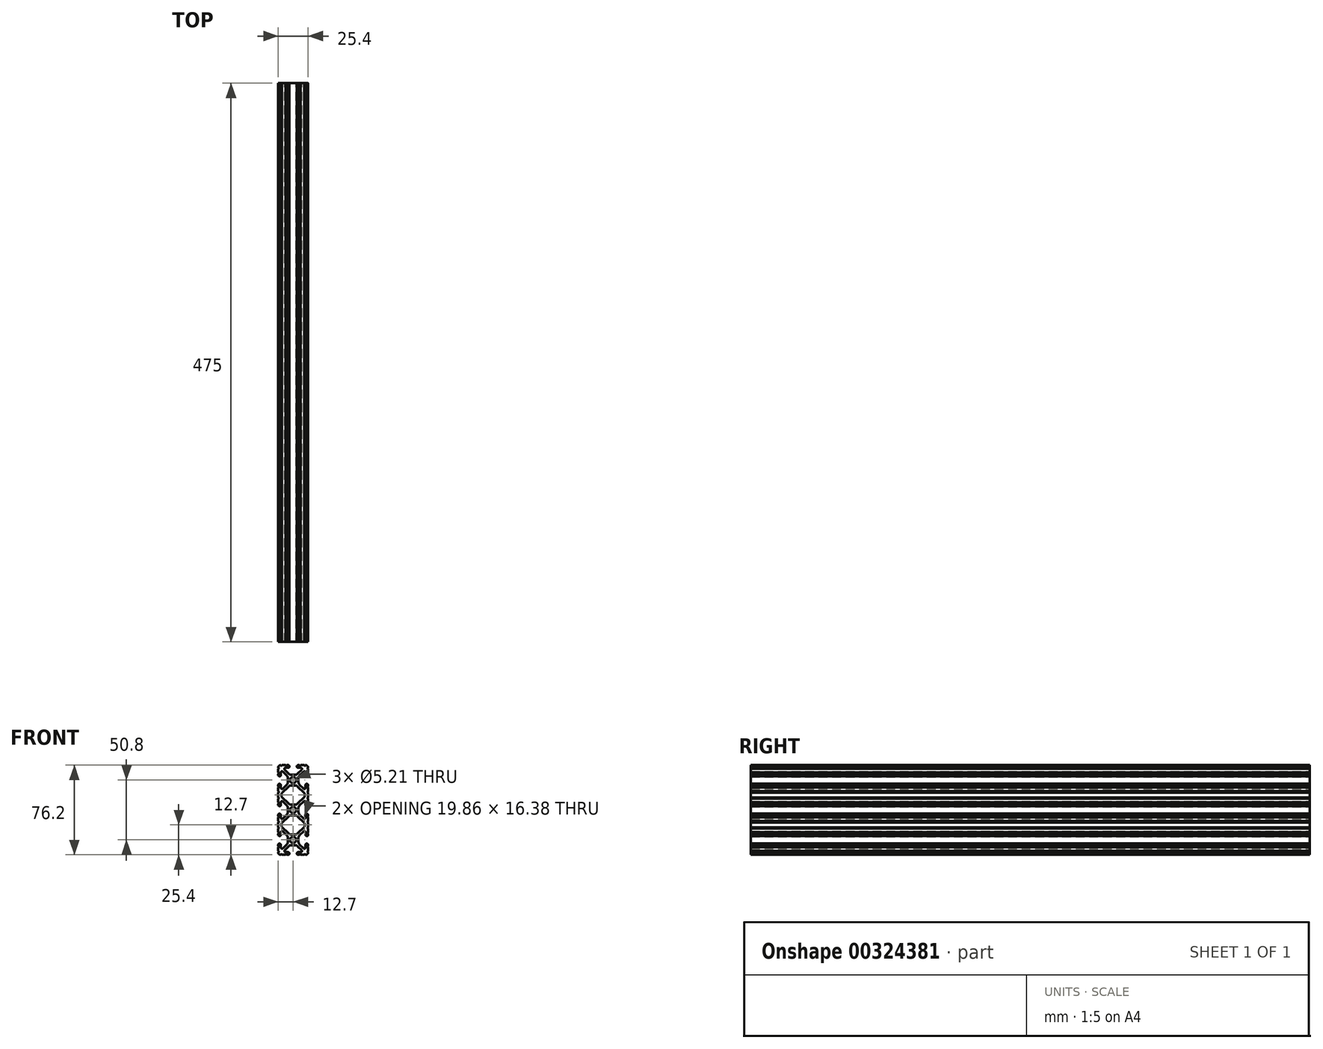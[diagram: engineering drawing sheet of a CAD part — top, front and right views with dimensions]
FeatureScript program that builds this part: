
annotation { "Feature Type Name" : "Feature", "Feature Type Description" : "" }
export const myFeature = defineFeature(function(context is Context, id is Id, definition is map)
    precondition{}
    {
        {
            var Q0;
            Q0=qCreatedBy(makeId("Front.planeOp"),FACE);
            var sketch = newSketch(context, id + "F0", { "sketchPlane" : qUnion([Q0])});
            skArc(sketch, "E0", {"start": v(2.6, 25.4) * mm, "mid": v(0, 28) * mm, "end": v(-2.6, 25.4) * mm});
            skArc(sketch, "E1", {"start": v(-2.6, 25.4) * mm, "mid": v(0, 22.8) * mm, "end": v(2.6, 25.4) * mm});
            skArc(sketch, "E2", {"start": v(-10.57, 38.1) * mm, "mid": v(-10.06, 37.6) * mm, "end": v(-9.55, 38.1) * mm});
            skArc(sketch, "E3", {"start": v(-10.57, 38.1) * mm, "mid": v(-12.08, 37.48) * mm, "end": v(-12.7, 35.97) * mm});
            skArc(sketch, "E4", {"start": v(-12.7, 34.95) * mm, "mid": v(-12.2, 35.46) * mm, "end": v(-12.7, 35.97) * mm});
            skLineSegment(sketch, "E5", {"start": v(-12.7, 34.95) * mm, "end": v(-12.7, 31.72) * mm});
            skArc(sketch, "E6", {"start": v(-12.7, 30.7) * mm, "mid": v(-12.2, 31.22) * mm, "end": v(-12.7, 31.72) * mm});
            skLineSegment(sketch, "E7", {"start": v(-12.7, 30.7) * mm, "end": v(-12.7, 29.7) * mm});
            skArc(sketch, "E8", {"start": v(-12.7, 29.7) * mm, "mid": v(-11.6, 28.6) * mm, "end": v(-10.5, 29.7) * mm});
            skLineSegment(sketch, "E9", {"start": v(-10.5, 29.7) * mm, "end": v(-10.5, 31.87) * mm});
            skArc(sketch, "E10", {"start": v(-8.76, 32.6) * mm, "mid": v(-9.86, 32.81) * mm, "end": v(-10.5, 31.87) * mm});
            skLineSegment(sketch, "E11", {"start": v(-8.76, 32.6) * mm, "end": v(-5.44, 29.28) * mm});
            skArc(sketch, "E12", {"start": v(-4.5, 27.03) * mm, "mid": v(-4.75, 28.25) * mm, "end": v(-5.44, 29.28) * mm});
            skLineSegment(sketch, "E13", {"start": v(-4.5, 27.03) * mm, "end": v(-4.5, 23.77) * mm});
            skArc(sketch, "E14", {"start": v(-5.44, 21.52) * mm, "mid": v(-4.75, 22.55) * mm, "end": v(-4.5, 23.77) * mm});
            skLineSegment(sketch, "E15", {"start": v(-5.44, 21.52) * mm, "end": v(-8.76, 18.2) * mm});
            skArc(sketch, "E16", {"start": v(-10.5, 18.93) * mm, "mid": v(-9.86, 17.99) * mm, "end": v(-8.76, 18.2) * mm});
            skLineSegment(sketch, "E17", {"start": v(-10.5, 18.93) * mm, "end": v(-10.5, 21.1) * mm});
            skArc(sketch, "E18", {"start": v(-10.5, 21.1) * mm, "mid": v(-11.6, 22.2) * mm, "end": v(-12.7, 21.1) * mm});
            skLineSegment(sketch, "E19", {"start": v(-12.7, 21.1) * mm, "end": v(-12.7, 20.1) * mm});
            skArc(sketch, "E20", {"start": v(-12.7, 19.08) * mm, "mid": v(-12.2, 19.58) * mm, "end": v(-12.7, 20.1) * mm});
            skLineSegment(sketch, "E21", {"start": v(-12.7, 19.08) * mm, "end": v(-12.7, 15.85) * mm});
            skArc(sketch, "E22", {"start": v(-12.7, 14.83) * mm, "mid": v(-12.2, 15.34) * mm, "end": v(-12.7, 15.85) * mm});
            skLineSegment(sketch, "E23", {"start": v(-12.7, 14.83) * mm, "end": v(-12.7, 10.57) * mm});
            skArc(sketch, "E24", {"start": v(-12.7, 9.55) * mm, "mid": v(-12.2, 10.06) * mm, "end": v(-12.7, 10.57) * mm});
            skLineSegment(sketch, "E25", {"start": v(-12.7, 9.55) * mm, "end": v(-12.7, 6.32) * mm});
            skArc(sketch, "E26", {"start": v(-12.7, 5.3) * mm, "mid": v(-12.2, 5.82) * mm, "end": v(-12.7, 6.32) * mm});
            skLineSegment(sketch, "E27", {"start": v(-12.7, 5.3) * mm, "end": v(-12.7, 4.3) * mm});
            skArc(sketch, "E28", {"start": v(-12.7, 4.3) * mm, "mid": v(-11.6, 3.2) * mm, "end": v(-10.5, 4.3) * mm});
            skLineSegment(sketch, "E29", {"start": v(-10.5, 4.3) * mm, "end": v(-10.5, 6.47) * mm});
            skArc(sketch, "E30", {"start": v(-8.76, 7.2) * mm, "mid": v(-9.86, 7.41) * mm, "end": v(-10.5, 6.47) * mm});
            skLineSegment(sketch, "E31", {"start": v(-8.76, 7.2) * mm, "end": v(-5.44, 3.88) * mm});
            skArc(sketch, "E32", {"start": v(-4.5, 1.63) * mm, "mid": v(-4.75, 2.85) * mm, "end": v(-5.44, 3.88) * mm});
            skLineSegment(sketch, "E33", {"start": v(-4.5, 1.63) * mm, "end": v(-4.5, -1.63) * mm});
            skArc(sketch, "E34", {"start": v(-5.44, -3.88) * mm, "mid": v(-4.75, -2.85) * mm, "end": v(-4.5, -1.63) * mm});
            skLineSegment(sketch, "E35", {"start": v(-5.44, -3.88) * mm, "end": v(-8.76, -7.2) * mm});
            skArc(sketch, "E36", {"start": v(-10.5, -6.47) * mm, "mid": v(-9.86, -7.41) * mm, "end": v(-8.76, -7.2) * mm});
            skLineSegment(sketch, "E37", {"start": v(-10.5, -6.47) * mm, "end": v(-10.5, -4.3) * mm});
            skArc(sketch, "E38", {"start": v(-10.5, -4.3) * mm, "mid": v(-11.6, -3.2) * mm, "end": v(-12.7, -4.3) * mm});
            skLineSegment(sketch, "E39", {"start": v(-12.7, -4.3) * mm, "end": v(-12.7, -5.3) * mm});
            skArc(sketch, "E40", {"start": v(-12.7, -6.32) * mm, "mid": v(-12.2, -5.82) * mm, "end": v(-12.7, -5.3) * mm});
            skLineSegment(sketch, "E41", {"start": v(-12.7, -6.32) * mm, "end": v(-12.7, -9.55) * mm});
            skArc(sketch, "E42", {"start": v(-12.7, -10.57) * mm, "mid": v(-12.2, -10.06) * mm, "end": v(-12.7, -9.55) * mm});
            skLineSegment(sketch, "E43", {"start": v(-12.7, -10.57) * mm, "end": v(-12.7, -14.83) * mm});
            skArc(sketch, "E44", {"start": v(-12.7, -15.85) * mm, "mid": v(-12.2, -15.34) * mm, "end": v(-12.7, -14.83) * mm});
            skLineSegment(sketch, "E45", {"start": v(-12.7, -15.85) * mm, "end": v(-12.7, -19.08) * mm});
            skArc(sketch, "E46", {"start": v(-12.7, -20.1) * mm, "mid": v(-12.2, -19.58) * mm, "end": v(-12.7, -19.08) * mm});
            skLineSegment(sketch, "E47", {"start": v(-12.7, -20.1) * mm, "end": v(-12.7, -21.1) * mm});
            skArc(sketch, "E48", {"start": v(-12.7, -21.1) * mm, "mid": v(-11.6, -22.2) * mm, "end": v(-10.5, -21.1) * mm});
            skLineSegment(sketch, "E49", {"start": v(-10.5, -21.1) * mm, "end": v(-10.5, -18.93) * mm});
            skArc(sketch, "E50", {"start": v(-8.76, -18.2) * mm, "mid": v(-9.86, -17.99) * mm, "end": v(-10.5, -18.93) * mm});
            skLineSegment(sketch, "E51", {"start": v(-8.76, -18.2) * mm, "end": v(-5.44, -21.52) * mm});
            skArc(sketch, "E52", {"start": v(-4.5, -23.77) * mm, "mid": v(-4.75, -22.55) * mm, "end": v(-5.44, -21.52) * mm});
            skLineSegment(sketch, "E53", {"start": v(-4.5, -23.77) * mm, "end": v(-4.5, -27.03) * mm});
            skArc(sketch, "E54", {"start": v(-5.44, -29.28) * mm, "mid": v(-4.75, -28.25) * mm, "end": v(-4.5, -27.03) * mm});
            skLineSegment(sketch, "E55", {"start": v(-5.44, -29.28) * mm, "end": v(-8.76, -32.6) * mm});
            skArc(sketch, "E56", {"start": v(-10.5, -31.87) * mm, "mid": v(-9.86, -32.81) * mm, "end": v(-8.76, -32.6) * mm});
            skLineSegment(sketch, "E57", {"start": v(-10.5, -31.87) * mm, "end": v(-10.5, -29.7) * mm});
            skArc(sketch, "E58", {"start": v(-10.5, -29.7) * mm, "mid": v(-11.6, -28.6) * mm, "end": v(-12.7, -29.7) * mm});
            skLineSegment(sketch, "E59", {"start": v(-12.7, -29.7) * mm, "end": v(-12.7, -30.7) * mm});
            skArc(sketch, "E60", {"start": v(-12.7, -31.72) * mm, "mid": v(-12.2, -31.22) * mm, "end": v(-12.7, -30.7) * mm});
            skLineSegment(sketch, "E61", {"start": v(-12.7, -31.72) * mm, "end": v(-12.7, -34.95) * mm});
            skArc(sketch, "E62", {"start": v(-12.7, -35.97) * mm, "mid": v(-12.2, -35.46) * mm, "end": v(-12.7, -34.95) * mm});
            skArc(sketch, "E63", {"start": v(-12.7, -35.97) * mm, "mid": v(-12.08, -37.48) * mm, "end": v(-10.57, -38.1) * mm});
            skArc(sketch, "E64", {"start": v(-9.55, -38.1) * mm, "mid": v(-10.06, -37.6) * mm, "end": v(-10.57, -38.1) * mm});
            skLineSegment(sketch, "E65", {"start": v(-9.55, -38.1) * mm, "end": v(-6.32, -38.1) * mm});
            skArc(sketch, "E66", {"start": v(-5.3, -38.1) * mm, "mid": v(-5.82, -37.6) * mm, "end": v(-6.32, -38.1) * mm});
            skLineSegment(sketch, "E67", {"start": v(-5.3, -38.1) * mm, "end": v(-4.3, -38.1) * mm});
            skArc(sketch, "E68", {"start": v(-4.3, -38.1) * mm, "mid": v(-3.2, -37) * mm, "end": v(-4.3, -35.9) * mm});
            skLineSegment(sketch, "E69", {"start": v(-4.3, -35.9) * mm, "end": v(-6.47, -35.9) * mm});
            skArc(sketch, "E70", {"start": v(-7.2, -34.16) * mm, "mid": v(-7.41, -35.26) * mm, "end": v(-6.47, -35.9) * mm});
            skLineSegment(sketch, "E71", {"start": v(-7.2, -34.16) * mm, "end": v(-3.88, -30.84) * mm});
            skArc(sketch, "E72", {"start": v(-1.63, -29.9) * mm, "mid": v(-2.85, -30.15) * mm, "end": v(-3.88, -30.84) * mm});
            skLineSegment(sketch, "E73", {"start": v(-1.63, -29.9) * mm, "end": v(1.63, -29.9) * mm});
            skArc(sketch, "E74", {"start": v(3.88, -30.84) * mm, "mid": v(2.85, -30.15) * mm, "end": v(1.63, -29.9) * mm});
            skLineSegment(sketch, "E75", {"start": v(3.88, -30.84) * mm, "end": v(7.2, -34.16) * mm});
            skArc(sketch, "E76", {"start": v(6.47, -35.9) * mm, "mid": v(7.41, -35.26) * mm, "end": v(7.2, -34.16) * mm});
            skLineSegment(sketch, "E77", {"start": v(6.47, -35.9) * mm, "end": v(4.3, -35.9) * mm});
            skArc(sketch, "E78", {"start": v(4.3, -35.9) * mm, "mid": v(3.2, -37) * mm, "end": v(4.3, -38.1) * mm});
            skLineSegment(sketch, "E79", {"start": v(4.3, -38.1) * mm, "end": v(5.3, -38.1) * mm});
            skArc(sketch, "E80", {"start": v(6.32, -38.1) * mm, "mid": v(5.82, -37.6) * mm, "end": v(5.3, -38.1) * mm});
            skLineSegment(sketch, "E81", {"start": v(6.32, -38.1) * mm, "end": v(9.55, -38.1) * mm});
            skArc(sketch, "E82", {"start": v(10.57, -38.1) * mm, "mid": v(10.06, -37.6) * mm, "end": v(9.55, -38.1) * mm});
            skArc(sketch, "E83", {"start": v(10.57, -38.1) * mm, "mid": v(12.08, -37.48) * mm, "end": v(12.7, -35.97) * mm});
            skArc(sketch, "E84", {"start": v(12.7, -34.95) * mm, "mid": v(12.2, -35.46) * mm, "end": v(12.7, -35.97) * mm});
            skLineSegment(sketch, "E85", {"start": v(12.7, -34.95) * mm, "end": v(12.7, -31.72) * mm});
            skArc(sketch, "E86", {"start": v(12.7, -30.7) * mm, "mid": v(12.2, -31.22) * mm, "end": v(12.7, -31.72) * mm});
            skLineSegment(sketch, "E87", {"start": v(12.7, -30.7) * mm, "end": v(12.7, -29.7) * mm});
            skArc(sketch, "E88", {"start": v(12.7, -29.7) * mm, "mid": v(11.6, -28.6) * mm, "end": v(10.5, -29.7) * mm});
            skLineSegment(sketch, "E89", {"start": v(10.5, -29.7) * mm, "end": v(10.5, -31.87) * mm});
            skArc(sketch, "E90", {"start": v(8.76, -32.6) * mm, "mid": v(9.86, -32.81) * mm, "end": v(10.5, -31.87) * mm});
            skLineSegment(sketch, "E91", {"start": v(8.76, -32.6) * mm, "end": v(5.44, -29.28) * mm});
            skArc(sketch, "E92", {"start": v(4.5, -27.03) * mm, "mid": v(4.75, -28.25) * mm, "end": v(5.44, -29.28) * mm});
            skLineSegment(sketch, "E93", {"start": v(4.5, -27.03) * mm, "end": v(4.5, -23.77) * mm});
            skArc(sketch, "E94", {"start": v(5.44, -21.52) * mm, "mid": v(4.75, -22.55) * mm, "end": v(4.5, -23.77) * mm});
            skLineSegment(sketch, "E95", {"start": v(5.44, -21.52) * mm, "end": v(8.76, -18.2) * mm});
            skArc(sketch, "E96", {"start": v(10.5, -18.93) * mm, "mid": v(9.86, -17.99) * mm, "end": v(8.76, -18.2) * mm});
            skLineSegment(sketch, "E97", {"start": v(10.5, -18.93) * mm, "end": v(10.5, -21.1) * mm});
            skArc(sketch, "E98", {"start": v(10.5, -21.1) * mm, "mid": v(11.6, -22.2) * mm, "end": v(12.7, -21.1) * mm});
            skLineSegment(sketch, "E99", {"start": v(12.7, -21.1) * mm, "end": v(12.7, -20.1) * mm});
            skArc(sketch, "E100", {"start": v(12.7, -19.08) * mm, "mid": v(12.2, -19.58) * mm, "end": v(12.7, -20.1) * mm});
            skLineSegment(sketch, "E101", {"start": v(12.7, -19.08) * mm, "end": v(12.7, -15.85) * mm});
            skArc(sketch, "E102", {"start": v(12.7, -14.83) * mm, "mid": v(12.2, -15.34) * mm, "end": v(12.7, -15.85) * mm});
            skLineSegment(sketch, "E103", {"start": v(12.7, -14.83) * mm, "end": v(12.7, -10.57) * mm});
            skArc(sketch, "E104", {"start": v(12.7, -9.55) * mm, "mid": v(12.2, -10.06) * mm, "end": v(12.7, -10.57) * mm});
            skLineSegment(sketch, "E105", {"start": v(12.7, -9.55) * mm, "end": v(12.7, -6.32) * mm});
            skArc(sketch, "E106", {"start": v(12.7, -5.3) * mm, "mid": v(12.2, -5.82) * mm, "end": v(12.7, -6.32) * mm});
            skLineSegment(sketch, "E107", {"start": v(12.7, -5.3) * mm, "end": v(12.7, -4.3) * mm});
            skArc(sketch, "E108", {"start": v(12.7, -4.3) * mm, "mid": v(11.6, -3.2) * mm, "end": v(10.5, -4.3) * mm});
            skLineSegment(sketch, "E109", {"start": v(10.5, -4.3) * mm, "end": v(10.5, -6.47) * mm});
            skArc(sketch, "E110", {"start": v(8.76, -7.2) * mm, "mid": v(9.86, -7.41) * mm, "end": v(10.5, -6.47) * mm});
            skLineSegment(sketch, "E111", {"start": v(8.76, -7.2) * mm, "end": v(5.44, -3.88) * mm});
            skArc(sketch, "E112", {"start": v(4.5, -1.63) * mm, "mid": v(4.75, -2.85) * mm, "end": v(5.44, -3.88) * mm});
            skLineSegment(sketch, "E113", {"start": v(4.5, -1.63) * mm, "end": v(4.5, 1.63) * mm});
            skArc(sketch, "E114", {"start": v(5.44, 3.88) * mm, "mid": v(4.75, 2.85) * mm, "end": v(4.5, 1.63) * mm});
            skLineSegment(sketch, "E115", {"start": v(5.44, 3.88) * mm, "end": v(8.76, 7.2) * mm});
            skArc(sketch, "E116", {"start": v(10.5, 6.47) * mm, "mid": v(9.86, 7.41) * mm, "end": v(8.76, 7.2) * mm});
            skLineSegment(sketch, "E117", {"start": v(10.5, 6.47) * mm, "end": v(10.5, 4.3) * mm});
            skArc(sketch, "E118", {"start": v(10.5, 4.3) * mm, "mid": v(11.6, 3.2) * mm, "end": v(12.7, 4.3) * mm});
            skLineSegment(sketch, "E119", {"start": v(12.7, 4.3) * mm, "end": v(12.7, 5.3) * mm});
            skArc(sketch, "E120", {"start": v(12.7, 6.32) * mm, "mid": v(12.2, 5.82) * mm, "end": v(12.7, 5.3) * mm});
            skLineSegment(sketch, "E121", {"start": v(12.7, 6.32) * mm, "end": v(12.7, 9.55) * mm});
            skArc(sketch, "E122", {"start": v(12.7, 10.57) * mm, "mid": v(12.2, 10.06) * mm, "end": v(12.7, 9.55) * mm});
            skLineSegment(sketch, "E123", {"start": v(12.7, 10.57) * mm, "end": v(12.7, 14.83) * mm});
            skArc(sketch, "E124", {"start": v(12.7, 15.85) * mm, "mid": v(12.2, 15.34) * mm, "end": v(12.7, 14.83) * mm});
            skLineSegment(sketch, "E125", {"start": v(12.7, 15.85) * mm, "end": v(12.7, 19.08) * mm});
            skArc(sketch, "E126", {"start": v(12.7, 20.1) * mm, "mid": v(12.2, 19.58) * mm, "end": v(12.7, 19.08) * mm});
            skLineSegment(sketch, "E127", {"start": v(12.7, 20.1) * mm, "end": v(12.7, 21.1) * mm});
            skArc(sketch, "E128", {"start": v(12.7, 21.1) * mm, "mid": v(11.6, 22.2) * mm, "end": v(10.5, 21.1) * mm});
            skLineSegment(sketch, "E129", {"start": v(10.5, 21.1) * mm, "end": v(10.5, 18.93) * mm});
            skArc(sketch, "E130", {"start": v(8.76, 18.2) * mm, "mid": v(9.86, 17.99) * mm, "end": v(10.5, 18.93) * mm});
            skLineSegment(sketch, "E131", {"start": v(8.76, 18.2) * mm, "end": v(5.44, 21.52) * mm});
            skArc(sketch, "E132", {"start": v(4.5, 23.77) * mm, "mid": v(4.75, 22.55) * mm, "end": v(5.44, 21.52) * mm});
            skLineSegment(sketch, "E133", {"start": v(4.5, 23.77) * mm, "end": v(4.5, 27.03) * mm});
            skArc(sketch, "E134", {"start": v(5.44, 29.28) * mm, "mid": v(4.75, 28.25) * mm, "end": v(4.5, 27.03) * mm});
            skLineSegment(sketch, "E135", {"start": v(5.44, 29.28) * mm, "end": v(8.76, 32.6) * mm});
            skArc(sketch, "E136", {"start": v(10.5, 31.87) * mm, "mid": v(9.86, 32.81) * mm, "end": v(8.76, 32.6) * mm});
            skLineSegment(sketch, "E137", {"start": v(10.5, 31.87) * mm, "end": v(10.5, 29.7) * mm});
            skArc(sketch, "E138", {"start": v(10.5, 29.7) * mm, "mid": v(11.6, 28.6) * mm, "end": v(12.7, 29.7) * mm});
            skLineSegment(sketch, "E139", {"start": v(12.7, 29.7) * mm, "end": v(12.7, 30.7) * mm});
            skArc(sketch, "E140", {"start": v(12.7, 31.72) * mm, "mid": v(12.2, 31.22) * mm, "end": v(12.7, 30.7) * mm});
            skLineSegment(sketch, "E141", {"start": v(12.7, 31.72) * mm, "end": v(12.7, 34.95) * mm});
            skArc(sketch, "E142", {"start": v(12.7, 35.97) * mm, "mid": v(12.2, 35.46) * mm, "end": v(12.7, 34.95) * mm});
            skArc(sketch, "E143", {"start": v(12.7, 35.97) * mm, "mid": v(12.08, 37.48) * mm, "end": v(10.57, 38.1) * mm});
            skArc(sketch, "E144", {"start": v(9.55, 38.1) * mm, "mid": v(10.06, 37.6) * mm, "end": v(10.57, 38.1) * mm});
            skLineSegment(sketch, "E145", {"start": v(9.55, 38.1) * mm, "end": v(6.32, 38.1) * mm});
            skArc(sketch, "E146", {"start": v(5.3, 38.1) * mm, "mid": v(5.82, 37.6) * mm, "end": v(6.32, 38.1) * mm});
            skLineSegment(sketch, "E147", {"start": v(5.3, 38.1) * mm, "end": v(4.3, 38.1) * mm});
            skArc(sketch, "E148", {"start": v(4.3, 38.1) * mm, "mid": v(3.2, 37) * mm, "end": v(4.3, 35.9) * mm});
            skLineSegment(sketch, "E149", {"start": v(4.3, 35.9) * mm, "end": v(6.47, 35.9) * mm});
            skArc(sketch, "E150", {"start": v(7.2, 34.16) * mm, "mid": v(7.41, 35.26) * mm, "end": v(6.47, 35.9) * mm});
            skLineSegment(sketch, "E151", {"start": v(7.2, 34.16) * mm, "end": v(3.88, 30.84) * mm});
            skArc(sketch, "E152", {"start": v(1.63, 29.9) * mm, "mid": v(2.85, 30.15) * mm, "end": v(3.88, 30.84) * mm});
            skLineSegment(sketch, "E153", {"start": v(1.63, 29.9) * mm, "end": v(-1.63, 29.9) * mm});
            skArc(sketch, "E154", {"start": v(-3.88, 30.84) * mm, "mid": v(-2.85, 30.15) * mm, "end": v(-1.63, 29.9) * mm});
            skLineSegment(sketch, "E155", {"start": v(-3.88, 30.84) * mm, "end": v(-7.2, 34.16) * mm});
            skArc(sketch, "E156", {"start": v(-6.47, 35.9) * mm, "mid": v(-7.41, 35.26) * mm, "end": v(-7.2, 34.16) * mm});
            skLineSegment(sketch, "E157", {"start": v(-6.47, 35.9) * mm, "end": v(-4.3, 35.9) * mm});
            skArc(sketch, "E158", {"start": v(-4.3, 35.9) * mm, "mid": v(-3.2, 37) * mm, "end": v(-4.3, 38.1) * mm});
            skLineSegment(sketch, "E159", {"start": v(-4.3, 38.1) * mm, "end": v(-5.3, 38.1) * mm});
            skArc(sketch, "E160", {"start": v(-6.32, 38.1) * mm, "mid": v(-5.82, 37.6) * mm, "end": v(-5.3, 38.1) * mm});
            skLineSegment(sketch, "E161", {"start": v(-6.32, 38.1) * mm, "end": v(-9.55, 38.1) * mm});
            skArc(sketch, "E162", {"start": v(2.6, 0) * mm, "mid": v(0, 2.6) * mm, "end": v(-2.6, 0) * mm});
            skArc(sketch, "E163", {"start": v(-2.6, 0) * mm, "mid": v(0, -2.6) * mm, "end": v(2.6, 0) * mm});
            skArc(sketch, "E164", {"start": v(2.6, -25.4) * mm, "mid": v(0, -22.8) * mm, "end": v(-2.6, -25.4) * mm});
            skArc(sketch, "E165", {"start": v(-2.6, -25.4) * mm, "mid": v(0, -28) * mm, "end": v(2.6, -25.4) * mm});
            skLineSegment(sketch, "E166", {"start": v(-3.88, -5.44) * mm, "end": v(-9.47, -11.03) * mm});
            skArc(sketch, "E167", {"start": v(-1.63, -4.5) * mm, "mid": v(-2.85, -4.75) * mm, "end": v(-3.88, -5.44) * mm});
            skLineSegment(sketch, "E168", {"start": v(1.63, -4.5) * mm, "end": v(-1.63, -4.5) * mm});
            skArc(sketch, "E169", {"start": v(3.88, -5.44) * mm, "mid": v(2.85, -4.75) * mm, "end": v(1.63, -4.5) * mm});
            skLineSegment(sketch, "E170", {"start": v(9.47, -11.03) * mm, "end": v(3.88, -5.44) * mm});
            skArc(sketch, "E171", {"start": v(9.93, -12.15) * mm, "mid": v(9.81, -11.54) * mm, "end": v(9.47, -11.03) * mm});
            skLineSegment(sketch, "E172", {"start": v(9.93, -13.25) * mm, "end": v(9.93, -12.15) * mm});
            skArc(sketch, "E173", {"start": v(9.47, -14.37) * mm, "mid": v(9.81, -13.86) * mm, "end": v(9.93, -13.25) * mm});
            skLineSegment(sketch, "E174", {"start": v(3.88, -19.96) * mm, "end": v(9.47, -14.37) * mm});
            skArc(sketch, "E175", {"start": v(1.63, -20.9) * mm, "mid": v(2.85, -20.65) * mm, "end": v(3.88, -19.96) * mm});
            skLineSegment(sketch, "E176", {"start": v(-1.63, -20.9) * mm, "end": v(1.63, -20.9) * mm});
            skArc(sketch, "E177", {"start": v(-3.88, -19.96) * mm, "mid": v(-2.85, -20.65) * mm, "end": v(-1.63, -20.9) * mm});
            skLineSegment(sketch, "E178", {"start": v(-9.47, -14.37) * mm, "end": v(-3.88, -19.96) * mm});
            skArc(sketch, "E179", {"start": v(-9.93, -13.25) * mm, "mid": v(-9.81, -13.86) * mm, "end": v(-9.47, -14.37) * mm});
            skLineSegment(sketch, "E180", {"start": v(-9.93, -12.15) * mm, "end": v(-9.93, -13.25) * mm});
            skArc(sketch, "E181", {"start": v(-9.47, -11.03) * mm, "mid": v(-9.81, -11.54) * mm, "end": v(-9.93, -12.15) * mm});
            skLineSegment(sketch, "E182", {"start": v(-3.88, 19.96) * mm, "end": v(-9.47, 14.37) * mm});
            skArc(sketch, "E183", {"start": v(-1.63, 20.9) * mm, "mid": v(-2.85, 20.65) * mm, "end": v(-3.88, 19.96) * mm});
            skLineSegment(sketch, "E184", {"start": v(1.63, 20.9) * mm, "end": v(-1.63, 20.9) * mm});
            skArc(sketch, "E185", {"start": v(3.88, 19.96) * mm, "mid": v(2.85, 20.65) * mm, "end": v(1.63, 20.9) * mm});
            skLineSegment(sketch, "E186", {"start": v(9.47, 14.37) * mm, "end": v(3.88, 19.96) * mm});
            skArc(sketch, "E187", {"start": v(9.93, 13.25) * mm, "mid": v(9.81, 13.86) * mm, "end": v(9.47, 14.37) * mm});
            skLineSegment(sketch, "E188", {"start": v(9.93, 12.15) * mm, "end": v(9.93, 13.25) * mm});
            skArc(sketch, "E189", {"start": v(9.47, 11.03) * mm, "mid": v(9.81, 11.54) * mm, "end": v(9.93, 12.15) * mm});
            skLineSegment(sketch, "E190", {"start": v(3.88, 5.44) * mm, "end": v(9.47, 11.03) * mm});
            skArc(sketch, "E191", {"start": v(1.63, 4.5) * mm, "mid": v(2.85, 4.75) * mm, "end": v(3.88, 5.44) * mm});
            skLineSegment(sketch, "E192", {"start": v(-1.63, 4.5) * mm, "end": v(1.63, 4.5) * mm});
            skArc(sketch, "E193", {"start": v(-3.88, 5.44) * mm, "mid": v(-2.85, 4.75) * mm, "end": v(-1.63, 4.5) * mm});
            skLineSegment(sketch, "E194", {"start": v(-9.47, 11.03) * mm, "end": v(-3.88, 5.44) * mm});
            skArc(sketch, "E195", {"start": v(-9.93, 12.15) * mm, "mid": v(-9.81, 11.54) * mm, "end": v(-9.47, 11.03) * mm});
            skLineSegment(sketch, "E196", {"start": v(-9.93, 13.25) * mm, "end": v(-9.93, 12.15) * mm});
            skArc(sketch, "E197", {"start": v(-9.47, 14.37) * mm, "mid": v(-9.81, 13.86) * mm, "end": v(-9.93, 13.25) * mm});
            skSolve(sketch);
        }
        {
            var Q0;
            Q0=makeQuery(id+"F0.imprint","IMPRINT",FACE,{"disambiguationData":[TD([[makeQuery(id+"F0.imprint","IMPRINT",EDGE,{"derivedFrom":sQuery(id+"F0.wireOp",EDGE,"E0")}),-1.0]])]});
            extrude(context, id + "F1", {"entities" : qUnion([Q0]), "depth" : 475 * mm});
        }
    });
